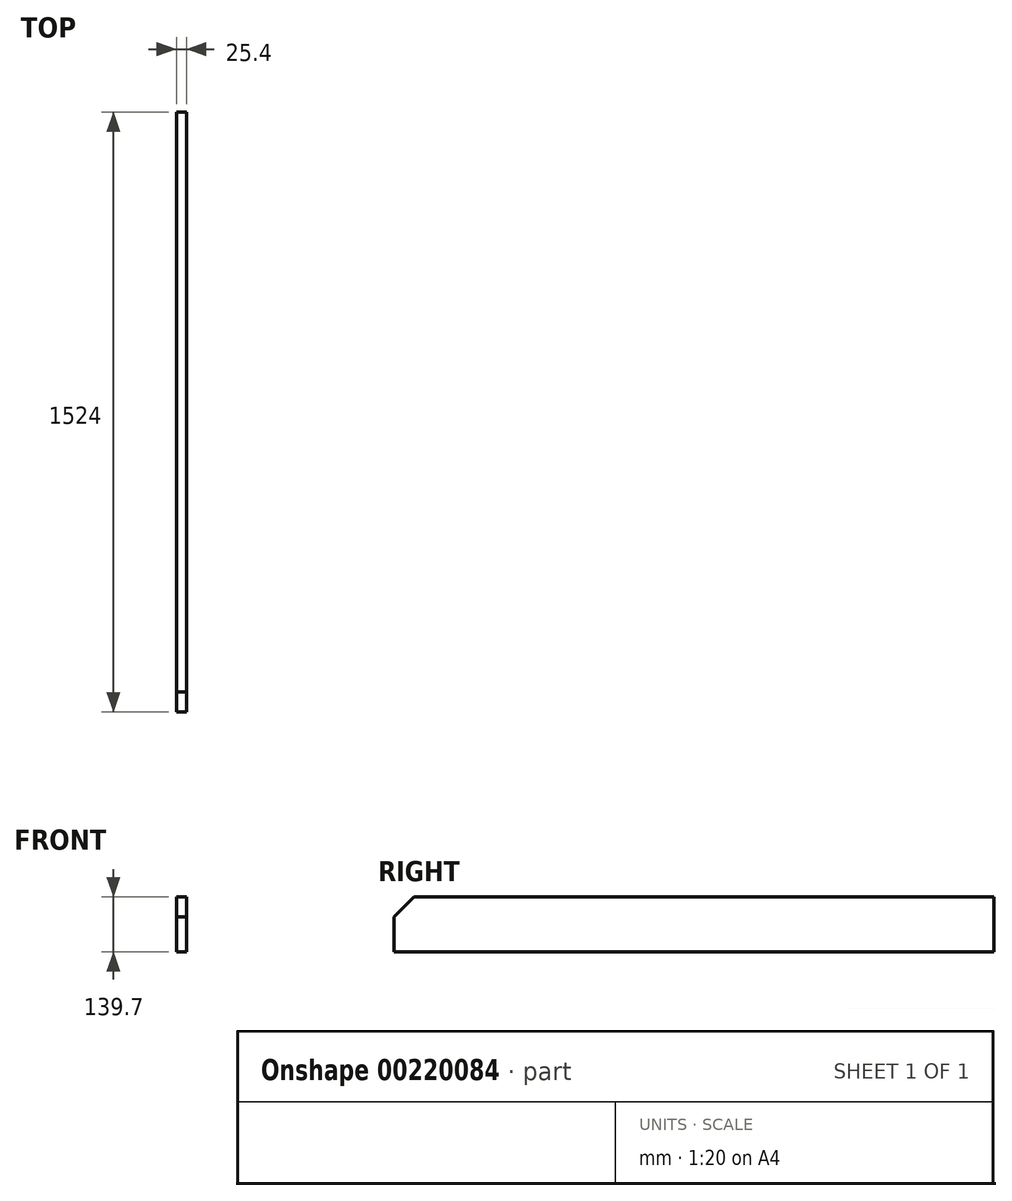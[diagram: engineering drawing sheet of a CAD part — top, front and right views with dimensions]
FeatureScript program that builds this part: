
annotation { "Feature Type Name" : "Feature", "Feature Type Description" : "" }
export const myFeature = defineFeature(function(context is Context, id is Id, definition is map)
    precondition{}
    {
        {
            var Q0;
            Q0=qCreatedBy(makeId("Front.planeOp"),FACE);
            var sketch = newSketch(context, id + "F0", { "sketchPlane" : qUnion([Q0])});
            skLineSegment(sketch, "E0.bottom", {"start": v(12.7, 69.85) * mm, "end": v(-12.7, 69.85) * mm});
            skLineSegment(sketch, "E0.top", {"start": v(12.7, -69.85) * mm, "end": v(-12.7, -69.85) * mm});
            skLineSegment(sketch, "E0.left", {"start": v(12.7, 69.85) * mm, "end": v(12.7, -69.85) * mm});
            skLineSegment(sketch, "E0.right", {"start": v(-12.7, 69.85) * mm, "end": v(-12.7, -69.85) * mm});
            skPoint(sketch, "E0.middle", {"position": v(0, 0) * mm});
            skSolve(sketch);
        }
        {
            var Q0;
            Q0 = qSketchRegion(id + "F0", true);
            extrude(context, id + "F1", {"entities" : qUnion([Q0]), "oppositeDirection" : true, "depth" : 1524 * mm});
        }
        {
            var Q0;
            Q0=makeQuery(id+"F1.opExtrude","CAP_EDGE",EDGE,{"disambiguationData":[OSD([sQuery(id+"F0.wireOp",EDGE,"E0.bottom")])],"isStart":true});
            chamfer(context, id + "F2", {"entities" : qUnion([Q0]), "width" : 50.8 * mm, "tangentPropagation" : true});
        }
    });
